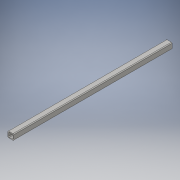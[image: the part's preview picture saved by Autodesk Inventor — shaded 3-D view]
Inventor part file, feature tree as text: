
AUTODESK INVENTOR PART (.ipt)
format: ipt  version: 2016 (Build 200138000, 138)  size: 113,664 bytes
history: native  units: in
note: dims shown in document units (in); Inventor stores cm internally (conversion verified against a paired STEP export)
features: extrude x1, sketch x1
ambient origin geometry x8: Origin, YZ Plane, XZ Plane, XY Plane, X Axis, Y Axis, Z Axis, Center Point
bodies: Solid1 (feature_tree)
feature tree (2):
  extrude  "Extrusion1"  Depth=1.0in
  sketch  "Sketch1"  dims[d0=1.0in d1=1.0in d2=0.125in d3=0.125in d4=27.0in d5=0.0in]
